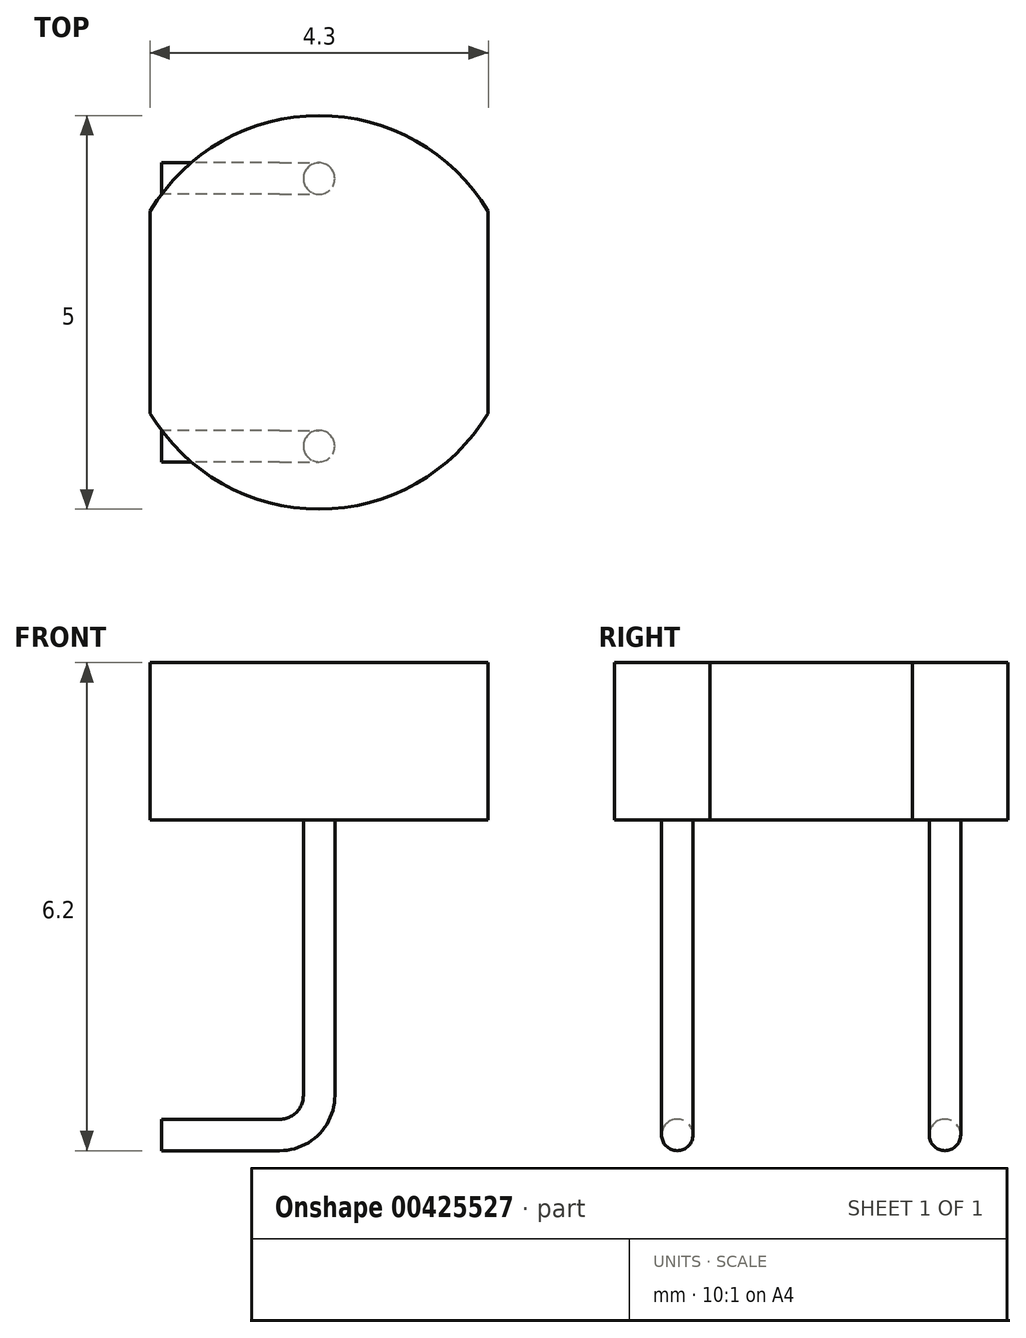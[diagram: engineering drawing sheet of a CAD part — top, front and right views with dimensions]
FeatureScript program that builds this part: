
annotation { "Feature Type Name" : "Feature", "Feature Type Description" : "" }
export const myFeature = defineFeature(function(context is Context, id is Id, definition is map)
    precondition{}
    {
        {
            var Q0;
            Q0=qCreatedBy(makeId("Top.planeOp"),FACE);
            var sketch = newSketch(context, id + "F0", { "sketchPlane" : qUnion([Q0])});
            skArc(sketch, "E0", {"start": v(-2.14, -1.28) * mm, "mid": v(0, -2.5) * mm, "end": v(2.15, -1.28) * mm});
            skLineSegment(sketch, "E1.top", {"start": v(2.15, -3.3) * mm, "end": v(-2.15, -3.3) * mm, "construction": true});
            skLineSegment(sketch, "E1.left", {"start": v(2.15, 1.28) * mm, "end": v(2.15, -1.28) * mm});
            skLineSegment(sketch, "E1.right", {"start": v(-2.14, 1.28) * mm, "end": v(-2.14, -1.28) * mm});
            skArc(sketch, "E2.trimOffspring", {"start": v(2.15, 1.28) * mm, "mid": v(0, 2.5) * mm, "end": v(-2.14, 1.28) * mm});
            skSolve(sketch);
        }
        {
            var Q0;
            Q0=qSketchRegion(id+"F0",true);
            extrude(context, id + "F1", {"entities" : qUnion([Q0]), "depth" : 2 * mm});
        }
        {
            var Q0;
            Q0=makeQuery(id+"F1.opExtrude","CAP_FACE",FACE,{"disambiguationData":[OSD([sQuery(id+"F0.wireOp",EDGE,"E0"),sQuery(id+"F0.wireOp",EDGE,"E1.left"),sQuery(id+"F0.wireOp",EDGE,"E1.right"),sQuery(id+"F0.wireOp",EDGE,"E2.trimOffspring")])],"isStart":true});
            var sketch = newSketch(context, id + "F2", { "sketchPlane" : qUnion([Q0])});
            skLineSegment(sketch, "E3", {"start": v(0, 0) * mm, "end": v(-4.1, 0) * mm, "construction": true});
            skLineSegment(sketch, "E4", {"start": v(0, -1.7) * mm, "end": v(-4.1, -1.7) * mm, "construction": true});
            skCircle(sketch, "E5", {"center": v(0, -1.7) * mm, "radius": 0.2 * mm});
            skCircle(sketch, "E6.MirrorC", {"center": v(0, 1.7) * mm, "radius": 0.2 * mm});
            skSolve(sketch);
        }
        {
            var Q0;
            Q0=qCreatedBy(makeId("Front.planeOp"),FACE);
            var sketch = newSketch(context, id + "F3", { "sketchPlane" : qUnion([Q0])});
            skLineSegment(sketch, "E7", {"start": v(0, 0) * mm, "end": v(0, -3.5) * mm});
            skLineSegment(sketch, "E8", {"start": v(-0.5, -4) * mm, "end": v(-2, -4) * mm});
            skPoint(sketch, "E9.visualSharp", {"position": v(0, -4) * mm});
            skArc(sketch, "E9.filletArc", {"start": v(-0.5, -4) * mm, "mid": v(-0.15, -3.85) * mm, "end": v(0, -3.5) * mm});
            skSolve(sketch);
        }
        {
            var Q0;
            Q0=qSketchRegion(id+"F2",true);
            var Q1;
            Q1=qConstructionFilter(qBodyType(qCreatedBy(id+"F3",EDGE),BodyType.WIRE),ConstructionObject.NO);
            sweep(context, id + "F4", {"operationType" : NewBodyOperationType.ADD, "profiles" : qUnion([Q0]), "path" : qUnion([Q1])});
        }
    });
